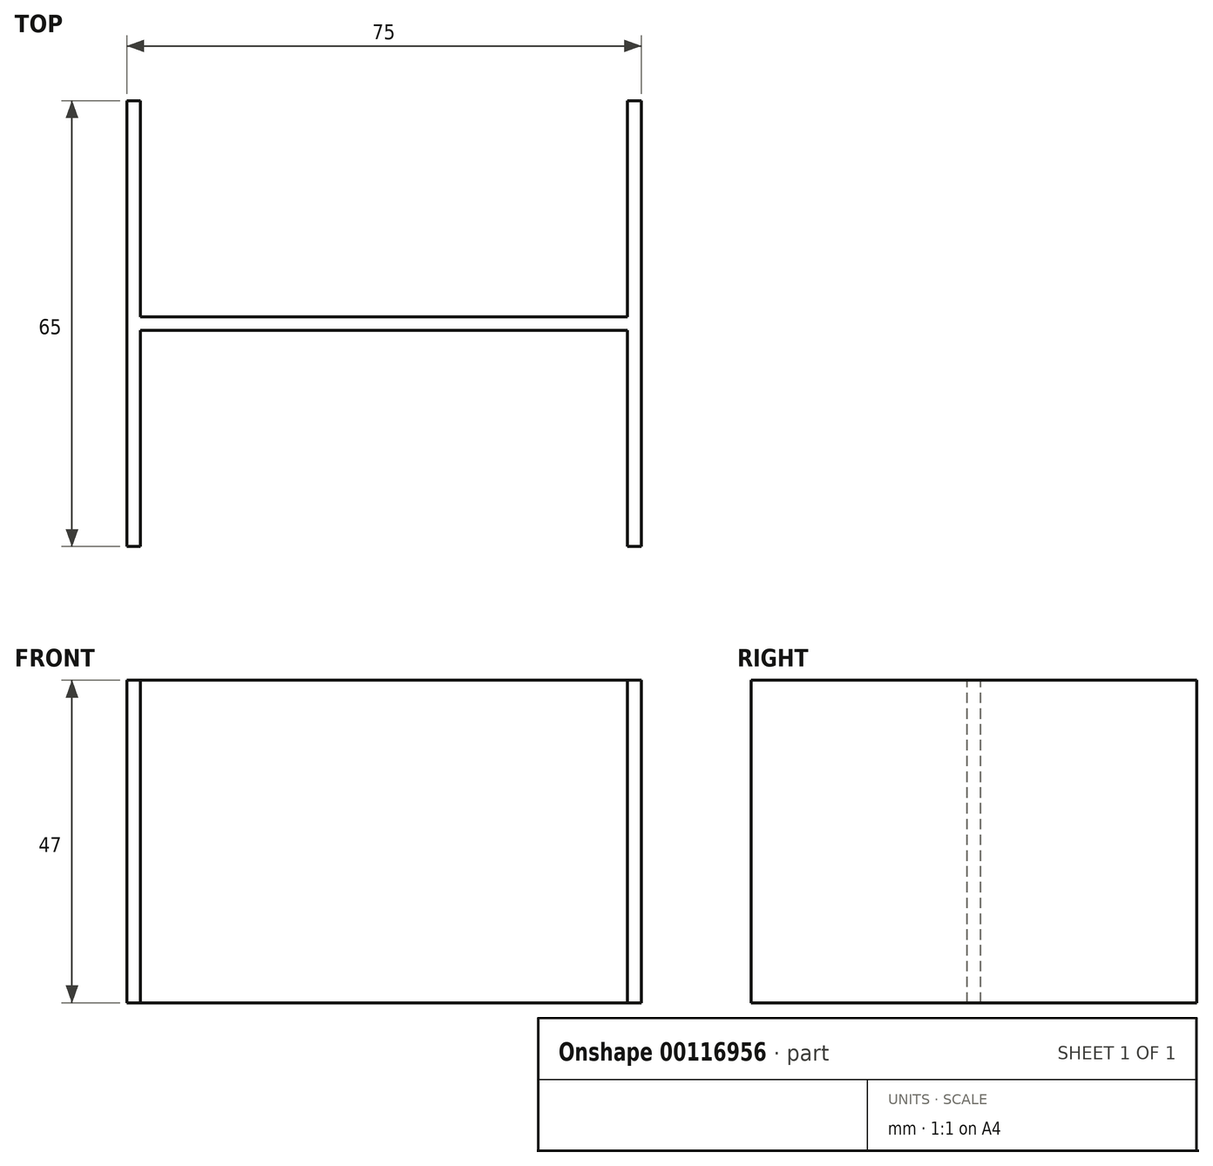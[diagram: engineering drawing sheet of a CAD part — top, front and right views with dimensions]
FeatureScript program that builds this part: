
annotation { "Feature Type Name" : "Feature", "Feature Type Description" : "" }
export const myFeature = defineFeature(function(context is Context, id is Id, definition is map)
    precondition{}
    {
        {
            var Q0;
            Q0=qCreatedBy(makeId("Top.planeOp"),FACE);
            var sketch = newSketch(context, id + "F0", { "sketchPlane" : qUnion([Q0])});
            skLineSegment(sketch, "E0.bottom", {"start": v(-37.5, 32.5) * mm, "end": v(37.5, 32.5) * mm});
            skLineSegment(sketch, "E0.top", {"start": v(-37.5, -32.5) * mm, "end": v(37.5, -32.5) * mm});
            skLineSegment(sketch, "E0.left", {"start": v(-37.5, 32.5) * mm, "end": v(-37.5, -32.5) * mm});
            skLineSegment(sketch, "E0.right", {"start": v(37.5, 32.5) * mm, "end": v(37.5, -32.5) * mm});
            skPoint(sketch, "E0.middle", {"position": v(0, 0) * mm});
            skSolve(sketch);
        }
        {
            var Q0;
            Q0 = qSketchRegion(id + "F0", true);
            extrude(context, id + "F1", {"entities" : qUnion([Q0]), "depth" : 47 * mm});
        }
        {
            var Q0;
            Q0=makeQuery(id+"F1.opExtrude","CAP_FACE",FACE,{"disambiguationData":[OSD([sQuery(id+"F0.wireOp",EDGE,"E0.bottom"),sQuery(id+"F0.wireOp",EDGE,"E0.top"),sQuery(id+"F0.wireOp",EDGE,"E0.left"),sQuery(id+"F0.wireOp",EDGE,"E0.right")])],"isStart":false});
            var sketch = newSketch(context, id + "F2", { "sketchPlane" : qUnion([Q0])});
            skLineSegment(sketch, "E1.bottom", {"start": v(-35.5, 1) * mm, "end": v(35.5, 1) * mm});
            skLineSegment(sketch, "E1.top", {"start": v(-35.5, 64) * mm, "end": v(35.5, 64) * mm});
            skLineSegment(sketch, "E1.left", {"start": v(-35.5, 1) * mm, "end": v(-35.5, 64) * mm});
            skLineSegment(sketch, "E1.right", {"start": v(35.5, 1) * mm, "end": v(35.5, 64) * mm});
            skPoint(sketch, "E1.middle", {"position": v(0, 32.5) * mm});
            skLineSegment(sketch, "E2.bottom", {"start": v(-35.5, -1) * mm, "end": v(35.5, -1) * mm});
            skLineSegment(sketch, "E2.top", {"start": v(-35.5, -64) * mm, "end": v(35.5, -64) * mm});
            skLineSegment(sketch, "E2.left", {"start": v(-35.5, -1) * mm, "end": v(-35.5, -64) * mm});
            skLineSegment(sketch, "E2.right", {"start": v(35.5, -1) * mm, "end": v(35.5, -64) * mm});
            skPoint(sketch, "E2.middle", {"position": v(0, -32.5) * mm});
            skSolve(sketch);
        }
        {
            var Q0;
            Q0 = qSketchRegion(id + "F2", true);
            extrude(context, id + "F3", {"entities" : qUnion([Q0]), "operationType" : NewBodyOperationType.REMOVE, "oppositeDirection" : true, "depth" : 66.72 * mm});
        }
    });
